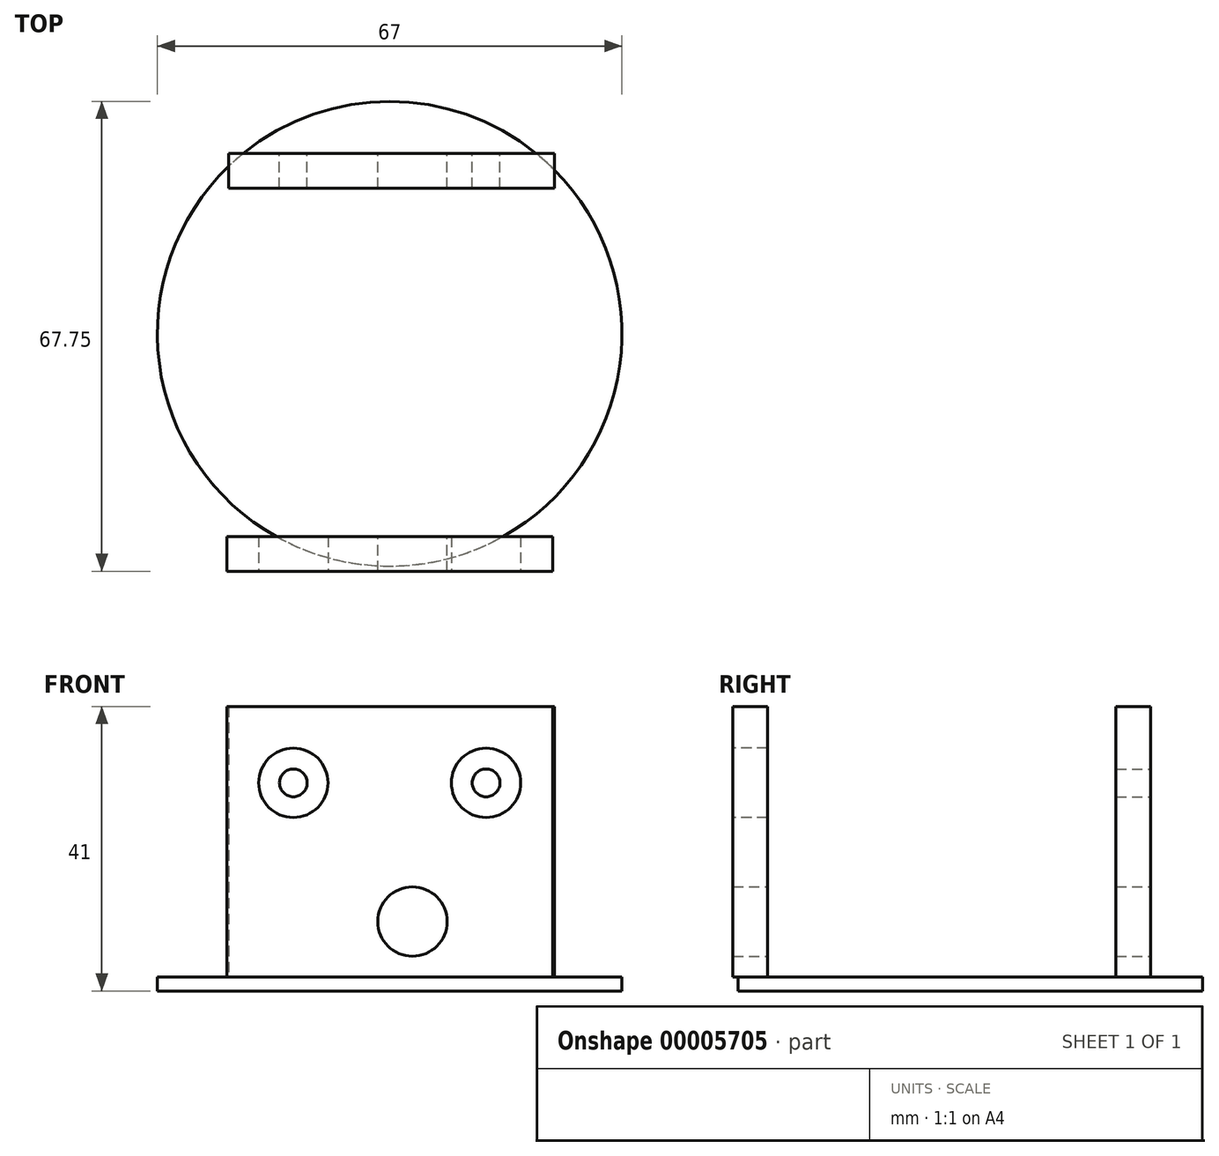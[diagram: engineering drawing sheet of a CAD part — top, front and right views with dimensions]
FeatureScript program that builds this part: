
annotation { "Feature Type Name" : "Feature", "Feature Type Description" : "" }
export const myFeature = defineFeature(function(context is Context, id is Id, definition is map)
    precondition{}
    {
        {
            var Q0;
            Q0=qCreatedBy(makeId("Top.planeOp"),FACE);
            var sketch = newSketch(context, id + "F0", { "sketchPlane" : qUnion([Q0])});
            skCircle(sketch, "E0", {"center": v(0, 0) * mm, "radius": 33.5 * mm});
            skSolve(sketch);
        }
        {
            var Q0;
            Q0=makeQuery(id+"F0.imprint","IMPRINT",FACE,{"disambiguationData":[TD([[makeQuery(id+"F0.imprint","IMPRINT",EDGE,{"derivedFrom":sQuery(id+"F0.wireOp",EDGE,"E0")}),1.0]])]});
            extrude(context, id + "F1", {"entities" : qUnion([Q0]), "depth" : 2 * mm});
        }
        {
            var Q0;
            Q0=makeQuery(id+"F1.opExtrude","CAP_FACE",FACE,{"disambiguationData":[OSD([sQuery(id+"F0.wireOp",EDGE,"E0")])],"isStart":false});
            var sketch = newSketch(context, id + "F2", { "sketchPlane" : qUnion([Q0])});
            skLineSegment(sketch, "E1.bottom", {"start": v(-23.22, 21) * mm, "end": v(23.78, 21) * mm});
            skLineSegment(sketch, "E1.top", {"start": v(-23.22, 26) * mm, "end": v(23.78, 26) * mm});
            skLineSegment(sketch, "E1.left", {"start": v(-23.22, 21) * mm, "end": v(-23.22, 26) * mm});
            skLineSegment(sketch, "E1.right", {"start": v(23.78, 21) * mm, "end": v(23.78, 26) * mm});
            skLineSegment(sketch, "E2.bottom", {"start": v(-23.5, -29.25) * mm, "end": v(23.5, -29.25) * mm});
            skLineSegment(sketch, "E2.top", {"start": v(-23.5, -34.25) * mm, "end": v(23.5, -34.25) * mm});
            skLineSegment(sketch, "E2.left", {"start": v(-23.5, -29.25) * mm, "end": v(-23.5, -34.25) * mm});
            skLineSegment(sketch, "E2.right", {"start": v(23.5, -29.25) * mm, "end": v(23.5, -34.25) * mm});
            skPoint(sketch, "E3", {"position": v(0, -29.25) * mm});
            skSolve(sketch);
        }
        {
            var Q0;
            {var subQ0=makeQuery(id+"F1.opExtrude","CAP_EDGE",EDGE,{"disambiguationData":[OSD([sQuery(id+"F0.wireOp",EDGE,"E0")])],"isStart":false});var subQ1=sQuery(id+"F2.wireOp",EDGE,"E1.left");var subQ3=sQuery(id+"F2.wireOp",EDGE,"E1.top");var subQ6=makeQuery(id+"F2.imprint","INTERSECT",VERTEX,{"derivedFrom":[subQ3,subQ1]});var subQ7=sQuery(id+"F2.wireOp",EDGE,"E1.right");var subQ11=makeQuery(id+"F2.imprint","INTERSECT",VERTEX,{"derivedFrom":[subQ3,subQ7]});var subQ12=sQuery(id+"F2.wireOp",EDGE,"E2.bottom");var subQ14=makeQuery(id+"F2.imprint","INTERSECT",VERTEX,{"disambiguationData":[OD(0.0)],"derivedFrom":[subQ0,subQ12]});var subQ18=sQuery(id+"F2.wireOp",EDGE,"E1.bottom");Q0=qUnion([makeQuery(id+"F2.imprint","IMPRINT",FACE,{"disambiguationData":[TD([[makeQuery(id+"F2.imprint","IMPRINT",EDGE,{"disambiguationData":[TD([[subQ6,-1.0]])],"derivedFrom":subQ3}),-1.0]])]}),makeQuery(id+"F2.imprint","IMPRINT",FACE,{"disambiguationData":[TD([[makeQuery(id+"F2.imprint","IMPRINT",EDGE,{"disambiguationData":[TD([[subQ11,1.0]])],"derivedFrom":subQ3}),-1.0]])]}),makeQuery(id+"F2.imprint","IMPRINT",FACE,{"disambiguationData":[TD([[makeQuery(id+"F2.imprint","IMPRINT",EDGE,{"derivedFrom":sQuery(id+"F2.wireOp",EDGE,"E2.top")}),1.0]])]}),makeQuery(id+"F2.imprint","IMPRINT",FACE,{"disambiguationData":[TD([[makeQuery(id+"F2.imprint","IMPRINT",EDGE,{"disambiguationData":[TD([[subQ14,-1.0]])],"derivedFrom":subQ12}),-1.0]])]}),makeQuery(id+"F2.imprint","IMPRINT",FACE,{"disambiguationData":[TD([[makeQuery(id+"F2.imprint","IMPRINT",EDGE,{"derivedFrom":subQ18}),1.0]])]})]);}
            extrude(context, id + "F3", {"entities" : qUnion([Q0]), "operationType" : NewBodyOperationType.ADD, "depth" : 39 * mm});
        }
        {
            var Q0;
            Q0=makeQuery(id+"F3.opExtrude","SWEPT_FACE",FACE,{"disambiguationData":[OSD([sQuery(id+"F2.wireOp",EDGE,"E1.top")])]});
            var sketch = newSketch(context, id + "F4", { "sketchPlane" : qUnion([Q0])});
            skPoint(sketch, "E4", {"position": v(-23.78, 21.5) * mm});
            skCircle(sketch, "E5", {"center": v(-3.28, 10) * mm, "radius": 5 * mm});
            skPoint(sketch, "E6", {"position": v(0, 2) * mm});
            skCircle(sketch, "E7", {"center": v(-13.9, 30) * mm, "radius": 2 * mm});
            skCircle(sketch, "E8", {"center": v(13.9, 30) * mm, "radius": 2 * mm});
            skSolve(sketch);
        }
        {
            var Q0;
            {Q0=qUnion([makeQuery(id+"F4.imprint","IMPRINT",FACE,{"disambiguationData":[TD([[makeQuery(id+"F4.imprint","IMPRINT",EDGE,{"derivedFrom":sQuery(id+"F4.wireOp",EDGE,"E5")}),1.0]])]}),makeQuery(id+"F4.imprint","IMPRINT",FACE,{"disambiguationData":[TD([[makeQuery(id+"F4.imprint","IMPRINT",EDGE,{"derivedFrom":sQuery(id+"F4.wireOp",EDGE,"E7")}),1.0]])]}),makeQuery(id+"F4.imprint","IMPRINT",FACE,{"disambiguationData":[TD([[makeQuery(id+"F4.imprint","IMPRINT",EDGE,{"derivedFrom":sQuery(id+"F4.wireOp",EDGE,"E8")}),1.0]])]})]);}
            extrude(context, id + "F5", {"entities" : qUnion([Q0]), "operationType" : NewBodyOperationType.REMOVE, "endBound" : BoundingType.THROUGH_ALL, "oppositeDirection" : true, "depth" : 25 * mm});
        }
        {
            var Q0;
            Q0=makeQuery(id+"F3.opExtrude","SWEPT_FACE",FACE,{"disambiguationData":[OSD([sQuery(id+"F2.wireOp",EDGE,"E2.top")])]});
            var sketch = newSketch(context, id + "F6", { "sketchPlane" : qUnion([Q0])});
            skCircle(sketch, "E9", {"center": v(-13.9, 30) * mm, "radius": 5 * mm});
            skCircle(sketch, "E10", {"center": v(13.9, 30) * mm, "radius": 5 * mm});
            skSolve(sketch);
        }
        {
            var Q0;
            {var subQ0=makeQuery(id+"F3.opExtrude","SWEPT_FACE",FACE,{"disambiguationData":[OSD([sQuery(id+"F2.wireOp",EDGE,"E2.top")])]});var subQ1=makeQuery(id+"F6.imprint","IMPRINT",EDGE,{"derivedFrom":makeQuery(id+"F5.boolean.opBoolean","INTERSECT",EDGE,{"derivedFrom":[subQ0,makeQuery(id+"F5.opExtrude","SWEPT_FACE",FACE,{"disambiguationData":[OSD([sQuery(id+"F4.wireOp",EDGE,"E7")])]})]})});var subQ2=makeQuery(id+"F6.imprint","IMPRINT",EDGE,{"derivedFrom":makeQuery(id+"F5.boolean.opBoolean","INTERSECT",EDGE,{"derivedFrom":[subQ0,makeQuery(id+"F5.opExtrude","SWEPT_FACE",FACE,{"disambiguationData":[OSD([sQuery(id+"F4.wireOp",EDGE,"E8")])]})]})});Q0=qUnion([makeQuery(id+"F6.imprint","IMPRINT",FACE,{"disambiguationData":[TD([[subQ1,-1.0]])]}),makeQuery(id+"F6.imprint","IMPRINT",FACE,{"disambiguationData":[TD([[subQ2,-1.0]])]}),makeQuery(id+"F6.imprint","IMPRINT",FACE,{"disambiguationData":[TD([[makeQuery(id+"F6.imprint","IMPRINT",EDGE,{"derivedFrom":sQuery(id+"F6.wireOp",EDGE,"E9")}),1.0]])]}),makeQuery(id+"F6.imprint","IMPRINT",FACE,{"disambiguationData":[TD([[makeQuery(id+"F6.imprint","IMPRINT",EDGE,{"derivedFrom":sQuery(id+"F6.wireOp",EDGE,"E10")}),1.0]])]})]);}
            extrude(context, id + "F7", {"entities" : qUnion([Q0]), "operationType" : NewBodyOperationType.REMOVE, "oppositeDirection" : true, "depth" : 25 * mm});
        }
    });
